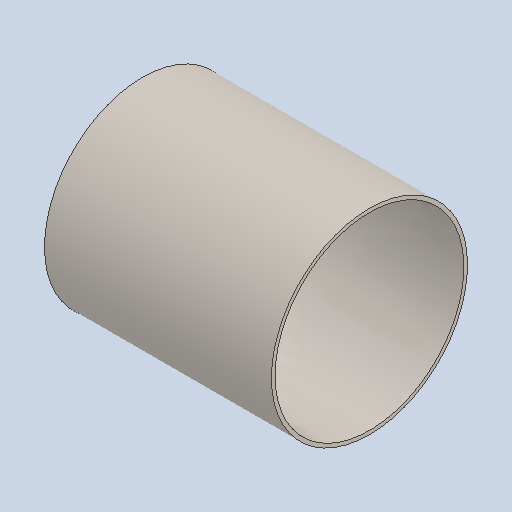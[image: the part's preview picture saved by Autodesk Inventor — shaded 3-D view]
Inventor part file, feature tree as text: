
AUTODESK INVENTOR PART (.ipt)
format: ipt  version: 2023 (Build 270158000, 158)  size: 112,128 bytes
history: native  units: in
note: dims shown in document units (in); Inventor stores cm internally (conversion verified against a paired STEP export)
features: extrude x1
ambient origin geometry x8: Origin, YZ Plane, XZ Plane, XY Plane, X Axis, Y Axis, Z Axis, Center Point
bodies: Solid1 (feature_tree)
feature tree (1):
  extrude  "Extrude-Thin1"  [1 undecoded]
note: 1 required parameter value undecoded (feature->parameter linkage not recoverable at this tier; creation-order binding heuristic only, values carry confidence <= 0.55)
